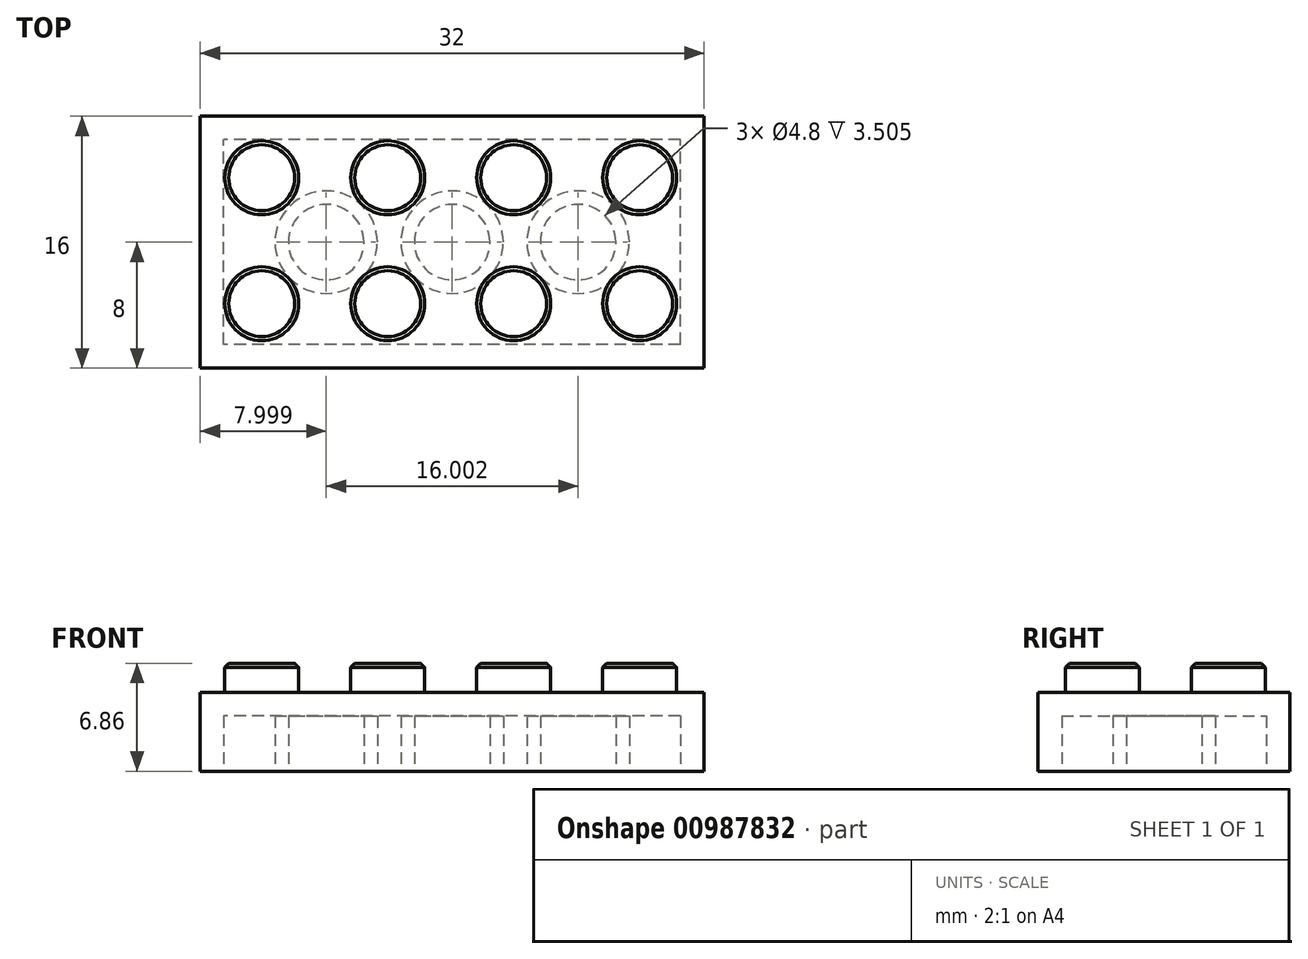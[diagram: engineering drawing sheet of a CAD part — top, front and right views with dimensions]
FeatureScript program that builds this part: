
annotation { "Feature Type Name" : "Feature", "Feature Type Description" : "" }
export const myFeature = defineFeature(function(context is Context, id is Id, definition is map)
    precondition{}
    {
        {
            var Q0;
            Q0=qCreatedBy(makeId("Top.planeOp"),FACE);
            var sketch = newSketch(context, id + "F0", { "sketchPlane" : qUnion([Q0])});
            skLineSegment(sketch, "E0.bottom", {"start": v(16, 8) * mm, "end": v(-16, 8) * mm});
            skLineSegment(sketch, "E0.top", {"start": v(16, -8) * mm, "end": v(-16, -8) * mm});
            skLineSegment(sketch, "E0.left", {"start": v(16, 8) * mm, "end": v(16, -8) * mm});
            skLineSegment(sketch, "E0.right", {"start": v(-16, 8) * mm, "end": v(-16, -8) * mm});
            skPoint(sketch, "E0.middle", {"position": v(0, 0) * mm});
            skSolve(sketch);
        }
        {
            var Q0;
            Q0=makeQuery(id+"F0.imprint","IMPRINT",FACE,{"disambiguationData":[TD([[makeQuery(id+"F0.imprint","IMPRINT",EDGE,{"derivedFrom":sQuery(id+"F0.wireOp",EDGE,"E0.bottom")}),1.0]])]});
            extrude(context, id + "F1", {"entities" : qUnion([Q0]), "depth" : 5 * mm, "offsetDistance" : 25.4 * mm});
        }
        {
            var Q0;
            Q0=makeQuery(id+"F1.opExtrude","CAP_FACE",FACE,{"disambiguationData":[OSD([sQuery(id+"F0.wireOp",EDGE,"E0.bottom"),sQuery(id+"F0.wireOp",EDGE,"E0.top"),sQuery(id+"F0.wireOp",EDGE,"E0.left"),sQuery(id+"F0.wireOp",EDGE,"E0.right")])],"isStart":false});
            var sketch = newSketch(context, id + "F2", { "sketchPlane" : qUnion([Q0])});
            skCircle(sketch, "E1", {"center": v(-12.1, 4.09) * mm, "radius": 2.35 * mm});
            skCircle(sketch, "E2.0.1.0", {"center": v(-12.1, -3.91) * mm, "radius": 2.35 * mm});
            skCircle(sketch, "E2.1.0.0", {"center": v(-4.09, 4.09) * mm, "radius": 2.35 * mm});
            skCircle(sketch, "E2.1.1.0", {"center": v(-4.09, -3.91) * mm, "radius": 2.35 * mm});
            skCircle(sketch, "E2.2.0.0", {"center": v(3.91, 4.09) * mm, "radius": 2.35 * mm});
            skCircle(sketch, "E2.2.1.0", {"center": v(3.91, -3.91) * mm, "radius": 2.35 * mm});
            skCircle(sketch, "E2.3.0.0", {"center": v(11.91, 4.09) * mm, "radius": 2.35 * mm});
            skCircle(sketch, "E2.3.1.0", {"center": v(11.91, -3.91) * mm, "radius": 2.35 * mm});
            skLineSegment(sketch, "E2.direction1", {"start": v(-12.1, 4.09) * mm, "end": v(-4.09, 4.09) * mm, "construction": true});
            skLineSegment(sketch, "E2.direction2", {"start": v(-12.1, 4.09) * mm, "end": v(-12.1, -3.91) * mm, "construction": true});
            skSolve(sketch);
        }
        {
            var Q0;
            Q0 = qSketchRegion(id + "F2", true);
            extrude(context, id + "F3", {"entities" : qUnion([Q0]), "operationType" : NewBodyOperationType.ADD, "depth" : 1.85 * mm, "offsetDistance" : 25.4 * mm});
        }
        {
            var Q0;
            Q0=makeQuery(id+"F1.opExtrude","CAP_FACE",FACE,{"disambiguationData":[OSD([sQuery(id+"F0.wireOp",EDGE,"E0.bottom"),sQuery(id+"F0.wireOp",EDGE,"E0.top"),sQuery(id+"F0.wireOp",EDGE,"E0.left"),sQuery(id+"F0.wireOp",EDGE,"E0.right")])],"isStart":true});
            var sketch = newSketch(context, id + "F4", { "sketchPlane" : qUnion([Q0])});
            skLineSegment(sketch, "E3.bottom", {"start": v(14.5, 6.5) * mm, "end": v(-14.5, 6.5) * mm});
            skLineSegment(sketch, "E3.top", {"start": v(14.5, -6.5) * mm, "end": v(-14.5, -6.5) * mm});
            skLineSegment(sketch, "E3.left", {"start": v(14.5, 6.5) * mm, "end": v(14.5, -6.5) * mm});
            skLineSegment(sketch, "E3.right", {"start": v(-14.5, 6.5) * mm, "end": v(-14.5, -6.5) * mm});
            skPoint(sketch, "E3.middle", {"position": v(0, 0) * mm});
            skCircle(sketch, "E4", {"center": v(-8, 0) * mm, "radius": 2.4 * mm});
            skCircle(sketch, "E5", {"center": v(-8, 0) * mm, "radius": 3.25 * mm});
            skCircle(sketch, "E6.1.0.0", {"center": v(0, 0) * mm, "radius": 2.4 * mm});
            skCircle(sketch, "E6.1.0.1", {"center": v(0, 0) * mm, "radius": 3.25 * mm});
            skCircle(sketch, "E6.2.0.0", {"center": v(8, 0) * mm, "radius": 2.4 * mm});
            skCircle(sketch, "E6.2.0.1", {"center": v(8, 0) * mm, "radius": 3.25 * mm});
            skLineSegment(sketch, "E6.direction1", {"start": v(-8, 0) * mm, "end": v(0, 0) * mm, "construction": true});
            skSolve(sketch);
        }
        {
            var Q0;
            Q0 = qSketchRegion(id + "F4", true);
            var Q1;
            Q1=makeQuery(id+"F4.imprint","IMPRINT",FACE,{"disambiguationData":[TD([[makeQuery(id+"F4.imprint","IMPRINT",EDGE,{"derivedFrom":sQuery(id+"F4.wireOp",EDGE,"E4")}),1.0]])]});
            var Q2;
            Q2=makeQuery(id+"F4.imprint","IMPRINT",FACE,{"disambiguationData":[TD([[makeQuery(id+"F4.imprint","IMPRINT",EDGE,{"derivedFrom":sQuery(id+"F4.wireOp",EDGE,"E6.2.0.0")}),1.0]])]});
            var Q3;
            Q3=makeQuery(id+"F4.imprint","IMPRINT",FACE,{"disambiguationData":[TD([[makeQuery(id+"F4.imprint","IMPRINT",EDGE,{"derivedFrom":sQuery(id+"F4.wireOp",EDGE,"E6.1.0.0")}),1.0]])]});
            extrude(context, id + "F5", {"entities" : qUnion([Q0, Q1, Q2, Q3]), "operationType" : NewBodyOperationType.REMOVE, "oppositeDirection" : true, "depth" : 3.5 * mm, "offsetDistance" : 25.4 * mm});
        }
        {
            var Q0;
            Q0=makeQuery(id+"F3.opExtrude","CAP_EDGE",EDGE,{"disambiguationData":[OSD([sQuery(id+"F2.wireOp",EDGE,"E1")])],"isStart":false});
            var Q1;
            Q1=makeQuery(id+"F3.opExtrude","CAP_EDGE",EDGE,{"disambiguationData":[OSD([sQuery(id+"F2.wireOp",EDGE,"E2.0.1.0")])],"isStart":false});
            var Q2;
            Q2=makeQuery(id+"F3.opExtrude","CAP_EDGE",EDGE,{"disambiguationData":[OSD([sQuery(id+"F2.wireOp",EDGE,"E2.1.1.0")])],"isStart":false});
            var Q3;
            Q3=makeQuery(id+"F3.opExtrude","CAP_EDGE",EDGE,{"disambiguationData":[OSD([sQuery(id+"F2.wireOp",EDGE,"E2.1.0.0")])],"isStart":false});
            var Q4;
            Q4=makeQuery(id+"F3.opExtrude","CAP_EDGE",EDGE,{"disambiguationData":[OSD([sQuery(id+"F2.wireOp",EDGE,"E2.2.0.0")])],"isStart":false});
            var Q5;
            Q5=makeQuery(id+"F3.opExtrude","CAP_EDGE",EDGE,{"disambiguationData":[OSD([sQuery(id+"F2.wireOp",EDGE,"E2.2.1.0")])],"isStart":false});
            var Q6;
            Q6=makeQuery(id+"F3.opExtrude","CAP_EDGE",EDGE,{"disambiguationData":[OSD([sQuery(id+"F2.wireOp",EDGE,"E2.3.1.0")])],"isStart":false});
            var Q7;
            Q7=makeQuery(id+"F3.opExtrude","CAP_EDGE",EDGE,{"disambiguationData":[OSD([sQuery(id+"F2.wireOp",EDGE,"E2.3.0.0")])],"isStart":false});
            chamfer(context, id + "F6", {"entities" : qUnion([Q0, Q1, Q2, Q3, Q4, Q5, Q6, Q7]), "width" : 0.25 * mm, "tangentPropagation" : true});
        }
    });
